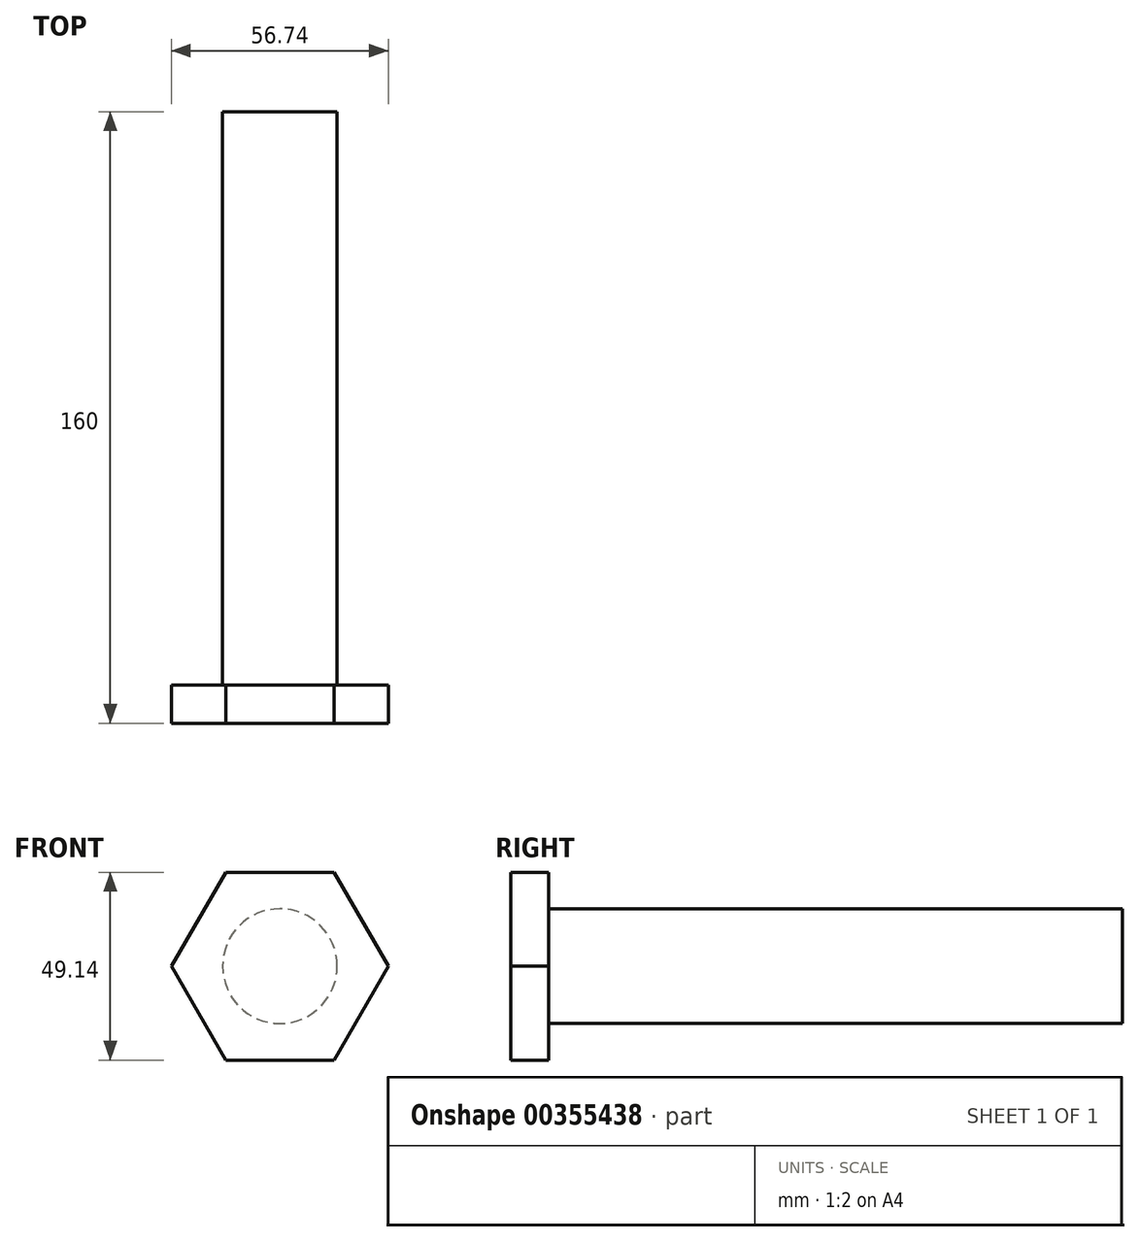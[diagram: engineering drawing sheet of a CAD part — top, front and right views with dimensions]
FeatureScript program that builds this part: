
annotation { "Feature Type Name" : "Feature", "Feature Type Description" : "" }
export const myFeature = defineFeature(function(context is Context, id is Id, definition is map)
    precondition{}
    {
        {
            var Q0;
            Q0=qCreatedBy(makeId("Front.planeOp"),FACE);
            var sketch = newSketch(context, id + "F0", { "sketchPlane" : qUnion([Q0])});
            skCircle(sketch, "E0", {"center": v(0, 0) * mm, "radius": 15 * mm});
            skSolve(sketch);
        }
        {
            var Q0;
            Q0=makeQuery(id+"F0.imprint","IMPRINT",FACE,{"disambiguationData":[TD([[makeQuery(id+"F0.imprint","IMPRINT",EDGE,{"derivedFrom":sQuery(id+"F0.wireOp",EDGE,"E0")}),1.0]])]});
            extrude(context, id + "F1", {"entities" : qUnion([Q0]), "endBound" : BoundingType.SYMMETRIC, "depth" : 150 * mm});
        }
        {
            var Q0;
            Q0=makeQuery(id+"F1.opExtrude","CAP_FACE",FACE,{"disambiguationData":[OSD([sQuery(id+"F0.wireOp",EDGE,"E0")])],"isStart":false});
            var sketch = newSketch(context, id + "F2", { "sketchPlane" : qUnion([Q0])});
            skCircle(sketch, "E1.cCircle", {"center": v(0, 0) * mm, "radius": 24.57 * mm, "construction": true});
            skLineSegment(sketch, "E1.0", {"start": v(14.18, 24.57) * mm, "end": v(28.37, 0) * mm});
            skLineSegment(sketch, "E1.1", {"start": v(28.37, 0) * mm, "end": v(14.18, -24.57) * mm});
            skLineSegment(sketch, "E1.2", {"start": v(14.18, -24.57) * mm, "end": v(-14.18, -24.57) * mm});
            skLineSegment(sketch, "E1.3", {"start": v(-14.18, -24.57) * mm, "end": v(-28.37, 0) * mm});
            skLineSegment(sketch, "E1.4", {"start": v(-28.37, 0) * mm, "end": v(-14.18, 24.57) * mm});
            skLineSegment(sketch, "E1.5", {"start": v(-14.18, 24.57) * mm, "end": v(14.18, 24.57) * mm});
            skPoint(sketch, "E1.0.midPoint", {"position": v(21.28, 12.28) * mm});
            skSolve(sketch);
        }
        {
            var Q0;
            Q0=qSketchRegion(id+"F2",true);
            extrude(context, id + "F3", {"entities" : qUnion([Q0]), "operationType" : NewBodyOperationType.ADD, "depth" : 10 * mm});
        }
    });
